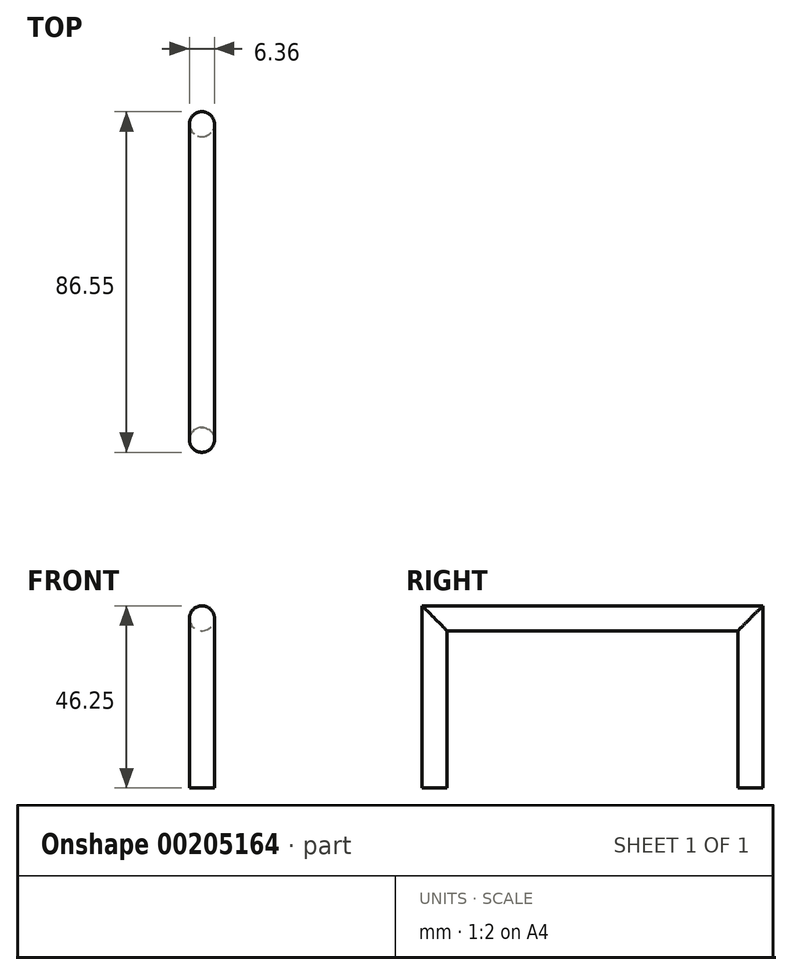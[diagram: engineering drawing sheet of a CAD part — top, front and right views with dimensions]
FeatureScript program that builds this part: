
annotation { "Feature Type Name" : "Feature", "Feature Type Description" : "" }
export const myFeature = defineFeature(function(context is Context, id is Id, definition is map)
    precondition{}
    {
        {
            var Q0;
            Q0=qCreatedBy(makeId("Right.planeOp"),FACE);
            var sketch = newSketch(context, id + "F0", { "sketchPlane" : qUnion([Q0])});
            skLineSegment(sketch, "E0", {"start": v(-39.6, 0) * mm, "end": v(-39.6, 43.07) * mm});
            skLineSegment(sketch, "E1", {"start": v(-39.6, 43.07) * mm, "end": v(40.6, 43.07) * mm});
            skLineSegment(sketch, "E2", {"start": v(40.6, 43.07) * mm, "end": v(40.6, 0) * mm});
            skSolve(sketch);
        }
        {
            var Q0;
            Q0=qCreatedBy(makeId("Top.planeOp"),FACE);
            var sketch = newSketch(context, id + "F1", { "sketchPlane" : qUnion([Q0])});
            skCircle(sketch, "E3", {"center": v(0, 40.6) * mm, "radius": 3.18 * mm});
            skSolve(sketch);
        }
        {
            var Q0;
            Q0=makeQuery(id+"F1.imprint","IMPRINT",FACE,{"disambiguationData":[TD([[makeQuery(id+"F1.imprint","IMPRINT",EDGE,{"derivedFrom":sQuery(id+"F1.wireOp",EDGE,"E3")}),1.0]])]});
            var Q1;
            Q1=sQuery(id+"F0.wireOp",EDGE,"E2");
            var Q2;
            Q2=sQuery(id+"F0.wireOp",EDGE,"E1");
            var Q3;
            Q3=sQuery(id+"F0.wireOp",EDGE,"E0");
            sweep(context, id + "F2", {"profiles" : qUnion([Q0]), "path" : qUnion([Q1, Q2, Q3])});
        }
    });
